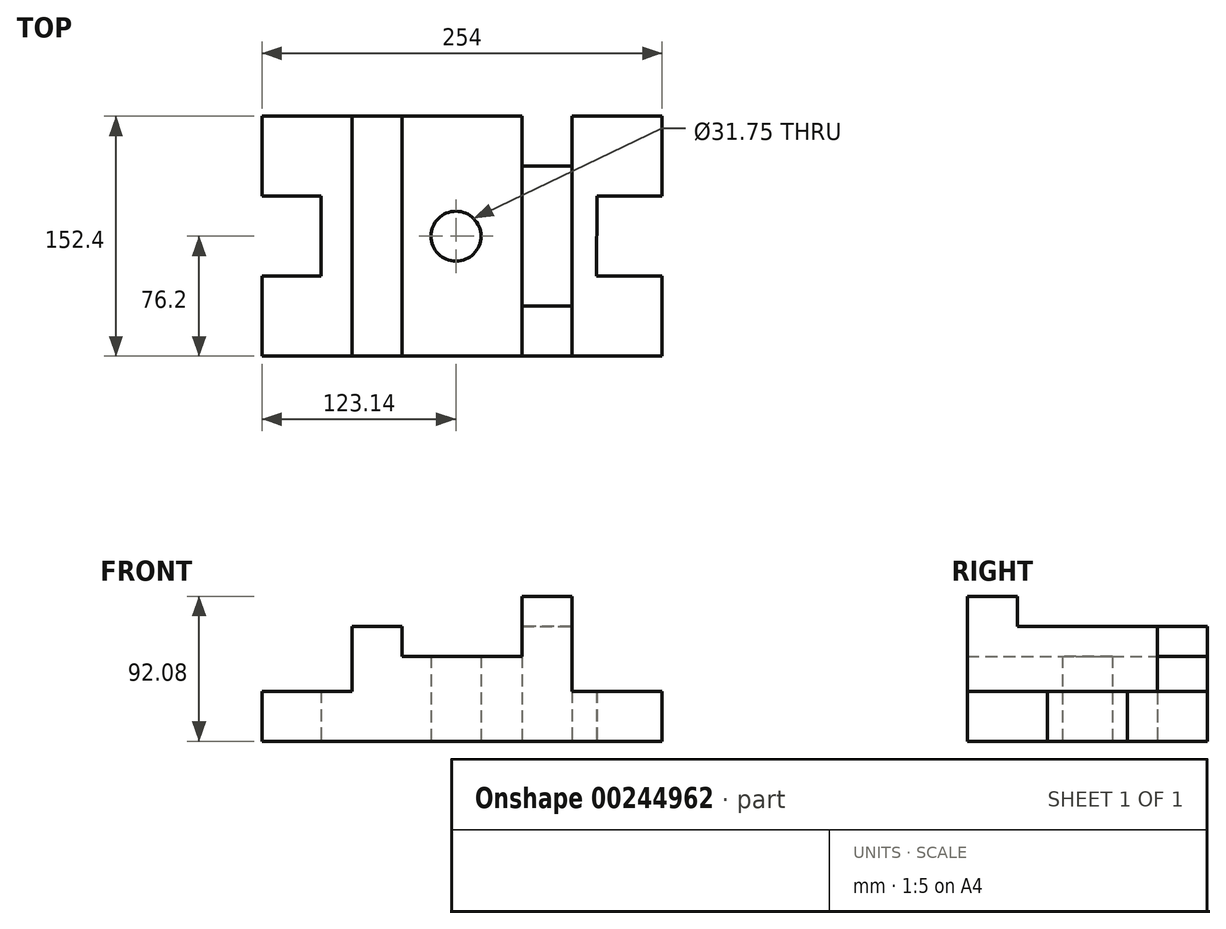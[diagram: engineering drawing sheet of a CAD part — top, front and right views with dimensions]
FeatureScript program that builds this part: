
annotation { "Feature Type Name" : "Feature", "Feature Type Description" : "" }
export const myFeature = defineFeature(function(context is Context, id is Id, definition is map)
    precondition{}
    {
        {
            var Q0;
            Q0=qCreatedBy(makeId("Top.planeOp"),FACE);
            var sketch = newSketch(context, id + "F0", { "sketchPlane" : qUnion([Q0])});
            skCircle(sketch, "E0", {"center": v(0, 0) * mm, "radius": 15.88 * mm});
            skLineSegment(sketch, "E1.bottom", {"start": v(-85.45, 76.2) * mm, "end": v(86, 76.2) * mm});
            skLineSegment(sketch, "E1.top", {"start": v(-85.73, -76.2) * mm, "end": v(85.72, -76.2) * mm});
            skLineSegment(sketch, "E1.left", {"start": v(-85.73, 25.4) * mm, "end": v(-85.72, -25.4) * mm});
            skLineSegment(sketch, "E2.bottom", {"start": v(89.3, -25.4) * mm, "end": v(130.86, -25.4) * mm});
            skLineSegment(sketch, "E2.top", {"start": v(89.59, -76.2) * mm, "end": v(130.86, -76.2) * mm});
            skLineSegment(sketch, "E2.right", {"start": v(130.86, -25.4) * mm, "end": v(130.86, -76.2) * mm});
            skLineSegment(sketch, "E3.bottom", {"start": v(86, 76.2) * mm, "end": v(130.85, 76.2) * mm});
            skLineSegment(sketch, "E3.top", {"start": v(89.58, 25.4) * mm, "end": v(130.85, 25.4) * mm});
            skLineSegment(sketch, "E3.right", {"start": v(130.85, 76.2) * mm, "end": v(130.85, 25.4) * mm});
            skLineSegment(sketch, "E4", {"start": v(89.58, 25.4) * mm, "end": v(89.3, -25.4) * mm});
            skLineSegment(sketch, "E5.bottom", {"start": v(-85.45, 76.2) * mm, "end": v(-123.14, 76.2) * mm});
            skLineSegment(sketch, "E5.top", {"start": v(-81.86, 25.4) * mm, "end": v(-123.14, 25.4) * mm});
            skLineSegment(sketch, "E5.right", {"start": v(-123.14, 76.2) * mm, "end": v(-123.14, 25.4) * mm});
            skLineSegment(sketch, "E6.bottom", {"start": v(-123.14, -25.4) * mm, "end": v(-85.73, -25.4) * mm});
            skLineSegment(sketch, "E6.top", {"start": v(-123.14, -76.2) * mm, "end": v(-85.73, -76.2) * mm});
            skLineSegment(sketch, "E6.left", {"start": v(-123.14, -25.4) * mm, "end": v(-123.14, -76.2) * mm});
            skLineSegment(sketch, "E7.trimOffspring", {"start": v(-85.72, -76.2) * mm, "end": v(-85.72, -76.22) * mm});
            skLineSegment(sketch, "E8", {"start": v(73.71, -76.2) * mm, "end": v(130.86, -76.2) * mm});
            skLineSegment(sketch, "E9", {"start": v(127.67, 76.5) * mm, "end": v(73.7, 76.2) * mm});
            skLineSegment(sketch, "E10", {"start": v(73.7, 76.2) * mm, "end": v(73.71, -76.2) * mm});
            skLineSegment(sketch, "E11", {"start": v(-123.14, 76.2) * mm, "end": v(-65.99, 76.2) * mm});
            skLineSegment(sketch, "E12", {"start": v(-65.99, 76.2) * mm, "end": v(-65.99, -76.2) * mm});
            skLineSegment(sketch, "E13", {"start": v(-65.99, 76.2) * mm, "end": v(-34.24, 76.2) * mm});
            skLineSegment(sketch, "E14", {"start": v(-34.24, 76.2) * mm, "end": v(-34.24, -76.2) * mm});
            skLineSegment(sketch, "E15", {"start": v(73.7, 76.2) * mm, "end": v(41.95, 76.2) * mm});
            skLineSegment(sketch, "E16", {"start": v(41.95, 76.2) * mm, "end": v(41.95, -76.2) * mm});
            skLineSegment(sketch, "E17", {"start": v(-65.99, 76.2) * mm, "end": v(-65.99, 44.45) * mm});
            skLineSegment(sketch, "E18", {"start": v(-65.99, 44.45) * mm, "end": v(-34.24, 44.45) * mm});
            skLineSegment(sketch, "E19", {"start": v(-65.99, -76.2) * mm, "end": v(-65.99, -44.45) * mm});
            skLineSegment(sketch, "E20", {"start": v(-65.99, -44.45) * mm, "end": v(-34.24, -44.45) * mm});
            skLineSegment(sketch, "E21", {"start": v(41.95, 44.45) * mm, "end": v(73.7, 44.45) * mm});
            skLineSegment(sketch, "E22", {"start": v(41.95, -44.45) * mm, "end": v(73.71, -44.45) * mm});
            skSolve(sketch);
        }
        {
            var Q0;
            Q0=makeQuery(id+"F0.imprint","IMPRINT",FACE,{"disambiguationData":[TD([[makeQuery(id+"F0.imprint","IMPRINT",EDGE,{"derivedFrom":sQuery(id+"F0.wireOp",EDGE,"E2.bottom")}),-1.0]])]});
            var Q1;
            {var subQ3=sQuery(id+"F0.wireOp",EDGE,"E1.left");Q1=makeQuery(id+"F0.imprint","IMPRINT",FACE,{"disambiguationData":[TD([[makeQuery(id+"F0.imprint","IMPRINT",EDGE,{"derivedFrom":subQ3}),1.0]])]});}
            var Q2;
            {var subQ3=sQuery(id+"F0.wireOp",EDGE,"E19");Q2=makeQuery(id+"F0.imprint","IMPRINT",FACE,{"disambiguationData":[TD([[makeQuery(id+"F0.imprint","IMPRINT",EDGE,{"derivedFrom":subQ3}),-1.0]])]});}
            var Q3;
            {var subQ5=sQuery(id+"F0.wireOp",EDGE,"E22");Q3=makeQuery(id+"F0.imprint","IMPRINT",FACE,{"disambiguationData":[TD([[makeQuery(id+"F0.imprint","IMPRINT",EDGE,{"derivedFrom":subQ5}),-1.0]])]});}
            var Q4;
            {var subQ0=sQuery(id+"F0.wireOp",EDGE,"E15");Q4=makeQuery(id+"F0.imprint","IMPRINT",FACE,{"disambiguationData":[TD([[makeQuery(id+"F0.imprint","IMPRINT",EDGE,{"derivedFrom":subQ0}),1.0]])]});}
            var Q5;
            Q5=makeQuery(id+"F0.imprint","IMPRINT",FACE,{"disambiguationData":[TD([[makeQuery(id+"F0.imprint","IMPRINT",EDGE,{"derivedFrom":sQuery(id+"F0.wireOp",EDGE,"E0")}),-1.0]])]});
            var Q6;
            {var subQ0=sQuery(id+"F0.wireOp",EDGE,"E13");Q6=makeQuery(id+"F0.imprint","IMPRINT",FACE,{"disambiguationData":[TD([[makeQuery(id+"F0.imprint","IMPRINT",EDGE,{"derivedFrom":subQ0}),-1.0]])]});}
            extrude(context, id + "F1", {"entities" : qUnion([Q0, Q1, Q2, Q3, Q4, Q5, Q6]), "depth" : 31.75 * mm});
        }
        {
            var Q0;
            Q0=makeQuery(id+"F0.imprint","IMPRINT",FACE,{"disambiguationData":[TD([[makeQuery(id+"F0.imprint","IMPRINT",EDGE,{"derivedFrom":sQuery(id+"F0.wireOp",EDGE,"E12")}),1.0]])]});
            var Q1;
            {var subQ0=sQuery(id+"F0.wireOp",EDGE,"E13");Q1=makeQuery(id+"F0.imprint","IMPRINT",FACE,{"disambiguationData":[TD([[makeQuery(id+"F0.imprint","IMPRINT",EDGE,{"derivedFrom":subQ0}),-1.0]])]});}
            var Q2;
            {var subQ3=sQuery(id+"F0.wireOp",EDGE,"E1.left");Q2=makeQuery(id+"F0.imprint","IMPRINT",FACE,{"disambiguationData":[TD([[makeQuery(id+"F0.imprint","IMPRINT",EDGE,{"derivedFrom":subQ3}),1.0]])]});}
            var Q3;
            {var subQ3=sQuery(id+"F0.wireOp",EDGE,"E19");Q3=makeQuery(id+"F0.imprint","IMPRINT",FACE,{"disambiguationData":[TD([[makeQuery(id+"F0.imprint","IMPRINT",EDGE,{"derivedFrom":subQ3}),-1.0]])]});}
            var Q4;
            Q4=makeQuery(id+"F0.imprint","IMPRINT",FACE,{"disambiguationData":[TD([[makeQuery(id+"F0.imprint","IMPRINT",EDGE,{"derivedFrom":sQuery(id+"F0.wireOp",EDGE,"E0")}),-1.0]])]});
            var Q5;
            {var subQ0=sQuery(id+"F0.wireOp",EDGE,"E21");Q5=makeQuery(id+"F0.imprint","IMPRINT",FACE,{"disambiguationData":[TD([[makeQuery(id+"F0.imprint","IMPRINT",EDGE,{"derivedFrom":subQ0}),-1.0]])]});}
            var Q6;
            {var subQ5=sQuery(id+"F0.wireOp",EDGE,"E22");Q6=makeQuery(id+"F0.imprint","IMPRINT",FACE,{"disambiguationData":[TD([[makeQuery(id+"F0.imprint","IMPRINT",EDGE,{"derivedFrom":subQ5}),-1.0]])]});}
            var Q7;
            Q7=makeQuery(id+"F0.imprint","IMPRINT",FACE,{"disambiguationData":[TD([[makeQuery(id+"F0.imprint","IMPRINT",EDGE,{"derivedFrom":sQuery(id+"F0.wireOp",EDGE,"E2.bottom")}),-1.0]])]});
            var Q8;
            {var subQ0=sQuery(id+"F0.wireOp",EDGE,"E15");Q8=makeQuery(id+"F0.imprint","IMPRINT",FACE,{"disambiguationData":[TD([[makeQuery(id+"F0.imprint","IMPRINT",EDGE,{"derivedFrom":subQ0}),1.0]])]});}
            extrude(context, id + "F2", {"entities" : qUnion([Q0, Q1, Q2, Q3, Q4, Q5, Q6, Q7, Q8]), "operationType" : NewBodyOperationType.ADD, "depth" : 31.75 * mm});
        }
        {
            var Q0;
            {var subQ0=sQuery(id+"F0.wireOp",EDGE,"E13");Q0=makeQuery(id+"F0.imprint","IMPRINT",FACE,{"disambiguationData":[TD([[makeQuery(id+"F0.imprint","IMPRINT",EDGE,{"derivedFrom":subQ0}),-1.0]])]});}
            var Q1;
            Q1=makeQuery(id+"F0.imprint","IMPRINT",FACE,{"disambiguationData":[TD([[makeQuery(id+"F0.imprint","IMPRINT",EDGE,{"derivedFrom":sQuery(id+"F0.wireOp",EDGE,"E12")}),1.0]])]});
            var Q2;
            {var subQ3=sQuery(id+"F0.wireOp",EDGE,"E19");Q2=makeQuery(id+"F0.imprint","IMPRINT",FACE,{"disambiguationData":[TD([[makeQuery(id+"F0.imprint","IMPRINT",EDGE,{"derivedFrom":subQ3}),-1.0]])]});}
            var Q3;
            Q3=makeQuery(id+"F0.imprint","IMPRINT",FACE,{"disambiguationData":[TD([[makeQuery(id+"F0.imprint","IMPRINT",EDGE,{"derivedFrom":sQuery(id+"F0.wireOp",EDGE,"E0")}),-1.0]])]});
            var Q4;
            {var subQ0=sQuery(id+"F0.wireOp",EDGE,"E21");Q4=makeQuery(id+"F0.imprint","IMPRINT",FACE,{"disambiguationData":[TD([[makeQuery(id+"F0.imprint","IMPRINT",EDGE,{"derivedFrom":subQ0}),-1.0]])]});}
            var Q5;
            {var subQ5=sQuery(id+"F0.wireOp",EDGE,"E22");Q5=makeQuery(id+"F0.imprint","IMPRINT",FACE,{"disambiguationData":[TD([[makeQuery(id+"F0.imprint","IMPRINT",EDGE,{"derivedFrom":subQ5}),-1.0]])]});}
            var Q6;
            {var subQ0=sQuery(id+"F0.wireOp",EDGE,"E15");Q6=makeQuery(id+"F0.imprint","IMPRINT",FACE,{"disambiguationData":[TD([[makeQuery(id+"F0.imprint","IMPRINT",EDGE,{"derivedFrom":subQ0}),1.0]])]});}
            extrude(context, id + "F3", {"entities" : qUnion([Q0, Q1, Q2, Q3, Q4, Q5, Q6]), "operationType" : NewBodyOperationType.ADD, "depth" : 53.97 * mm});
        }
        {
            var Q0;
            {var subQ3=sQuery(id+"F0.wireOp",EDGE,"E19");Q0=makeQuery(id+"F0.imprint","IMPRINT",FACE,{"disambiguationData":[TD([[makeQuery(id+"F0.imprint","IMPRINT",EDGE,{"derivedFrom":subQ3}),-1.0]])]});}
            var Q1;
            Q1=makeQuery(id+"F0.imprint","IMPRINT",FACE,{"disambiguationData":[TD([[makeQuery(id+"F0.imprint","IMPRINT",EDGE,{"derivedFrom":sQuery(id+"F0.wireOp",EDGE,"E12")}),1.0]])]});
            var Q2;
            {var subQ0=sQuery(id+"F0.wireOp",EDGE,"E13");Q2=makeQuery(id+"F0.imprint","IMPRINT",FACE,{"disambiguationData":[TD([[makeQuery(id+"F0.imprint","IMPRINT",EDGE,{"derivedFrom":subQ0}),-1.0]])]});}
            var Q3;
            {var subQ0=sQuery(id+"F0.wireOp",EDGE,"E15");Q3=makeQuery(id+"F0.imprint","IMPRINT",FACE,{"disambiguationData":[TD([[makeQuery(id+"F0.imprint","IMPRINT",EDGE,{"derivedFrom":subQ0}),1.0]])]});}
            var Q4;
            {var subQ0=sQuery(id+"F0.wireOp",EDGE,"E21");Q4=makeQuery(id+"F0.imprint","IMPRINT",FACE,{"disambiguationData":[TD([[makeQuery(id+"F0.imprint","IMPRINT",EDGE,{"derivedFrom":subQ0}),-1.0]])]});}
            var Q5;
            {var subQ5=sQuery(id+"F0.wireOp",EDGE,"E22");Q5=makeQuery(id+"F0.imprint","IMPRINT",FACE,{"disambiguationData":[TD([[makeQuery(id+"F0.imprint","IMPRINT",EDGE,{"derivedFrom":subQ5}),-1.0]])]});}
            extrude(context, id + "F4", {"entities" : qUnion([Q0, Q1, Q2, Q3, Q4, Q5]), "operationType" : NewBodyOperationType.ADD, "depth" : 73.02 * mm});
        }
        {
            var Q0;
            {var subQ0=sQuery(id+"F0.wireOp",EDGE,"E13");Q0=makeQuery(id+"F0.imprint","IMPRINT",FACE,{"disambiguationData":[TD([[makeQuery(id+"F0.imprint","IMPRINT",EDGE,{"derivedFrom":subQ0}),-1.0]])]});}
            var Q1;
            {var subQ3=sQuery(id+"F0.wireOp",EDGE,"E19");Q1=makeQuery(id+"F0.imprint","IMPRINT",FACE,{"disambiguationData":[TD([[makeQuery(id+"F0.imprint","IMPRINT",EDGE,{"derivedFrom":subQ3}),-1.0]])]});}
            var Q2;
            {var subQ5=sQuery(id+"F0.wireOp",EDGE,"E22");Q2=makeQuery(id+"F0.imprint","IMPRINT",FACE,{"disambiguationData":[TD([[makeQuery(id+"F0.imprint","IMPRINT",EDGE,{"derivedFrom":subQ5}),-1.0]])]});}
            var Q3;
            {var subQ0=sQuery(id+"F0.wireOp",EDGE,"E15");Q3=makeQuery(id+"F0.imprint","IMPRINT",FACE,{"disambiguationData":[TD([[makeQuery(id+"F0.imprint","IMPRINT",EDGE,{"derivedFrom":subQ0}),1.0]])]});}
            extrude(context, id + "F5", {"entities" : qUnion([Q0, Q1, Q2, Q3]), "operationType" : NewBodyOperationType.ADD, "depth" : 92.07 * mm});
        }
    });
